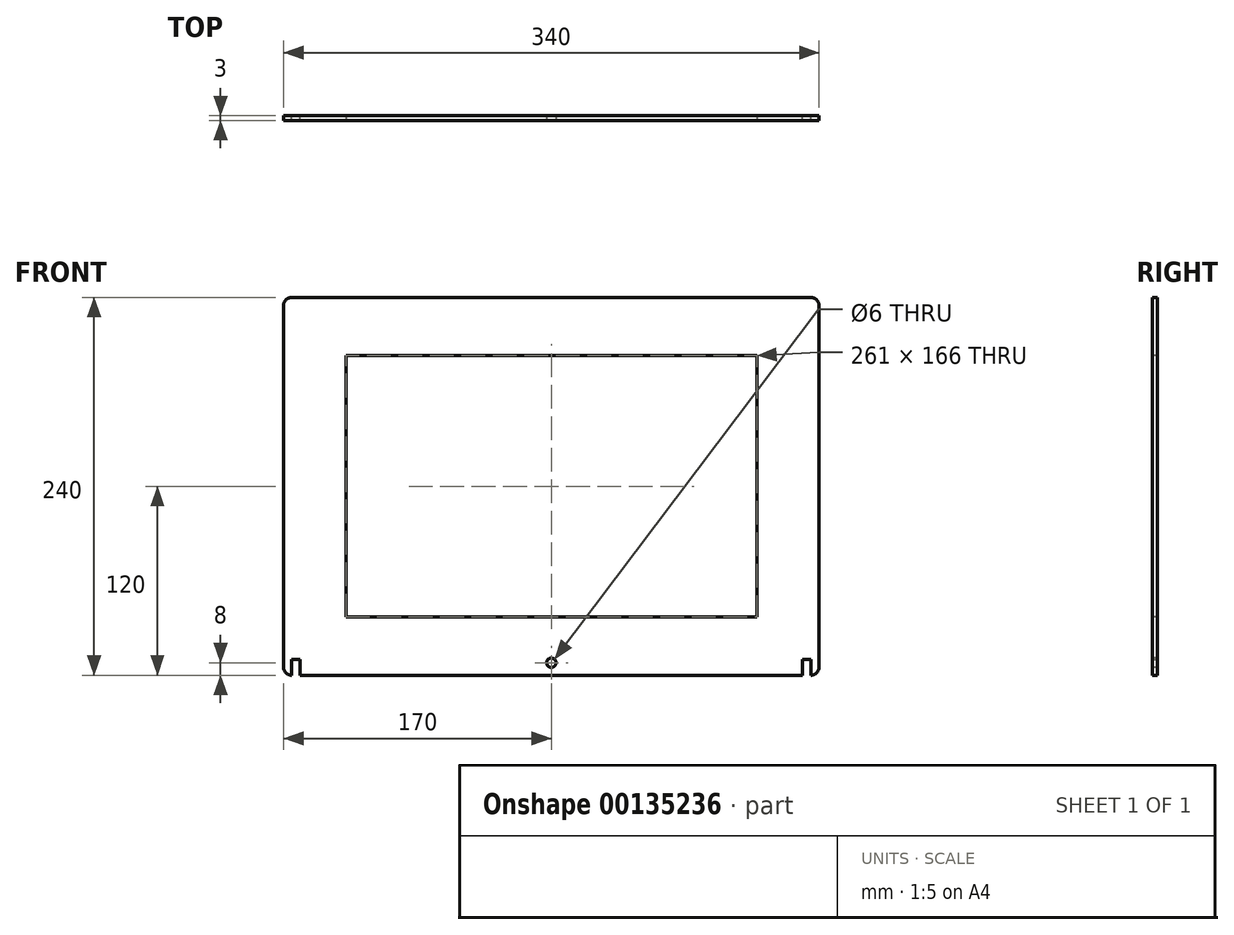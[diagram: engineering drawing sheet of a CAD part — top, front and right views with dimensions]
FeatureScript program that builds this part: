
annotation { "Feature Type Name" : "Feature", "Feature Type Description" : "" }
export const myFeature = defineFeature(function(context is Context, id is Id, definition is map)
    precondition{}
    {
        {
            var Q0;
            Q0=qCreatedBy(makeId("Front.planeOp"),FACE);
            var sketch = newSketch(context, id + "F0", { "sketchPlane" : qUnion([Q0])});
            skLineSegment(sketch, "E0.top", {"start": v(170, 120) * mm, "end": v(-170, 120) * mm});
            skLineSegment(sketch, "E0.left", {"start": v(170, -120) * mm, "end": v(170, 120) * mm});
            skLineSegment(sketch, "E0.right", {"start": v(-170, -120) * mm, "end": v(-170, 120) * mm});
            skPoint(sketch, "E0.middle", {"position": v(0, 0) * mm});
            skLineSegment(sketch, "E1", {"start": v(-165, -120) * mm, "end": v(-165, -110) * mm});
            skLineSegment(sketch, "E2", {"start": v(-165, -110) * mm, "end": v(-159.5, -110) * mm});
            skLineSegment(sketch, "E3", {"start": v(-159.5, -110) * mm, "end": v(-159.5, -120) * mm});
            skLineSegment(sketch, "E4.trimOffspring", {"start": v(-165, -120) * mm, "end": v(-170, -120) * mm});
            skLineSegment(sketch, "E5", {"start": v(165, -120) * mm, "end": v(165, -110) * mm});
            skLineSegment(sketch, "E6", {"start": v(165, -110) * mm, "end": v(159.5, -110) * mm});
            skLineSegment(sketch, "E7", {"start": v(159.5, -110) * mm, "end": v(159.5, -120) * mm});
            skLineSegment(sketch, "E8.trimOffspring", {"start": v(159.5, -120) * mm, "end": v(-159.5, -120) * mm});
            skLineSegment(sketch, "E9", {"start": v(170, -120) * mm, "end": v(165, -120) * mm});
            skSolve(sketch);
        }
        {
            var Q0;
            Q0 = qSketchRegion(id + "F0", true);
            extrude(context, id + "F1", {"entities" : qUnion([Q0]), "depth" : 3 * mm});
        }
        {
            var Q0;
            Q0=makeQuery(id+"F1.opExtrude","CAP_FACE",FACE,{"disambiguationData":[OSD([sQuery(id+"F0.wireOp",EDGE,"E0.bottom"),sQuery(id+"F0.wireOp",EDGE,"E0.top"),sQuery(id+"F0.wireOp",EDGE,"E0.left"),sQuery(id+"F0.wireOp",EDGE,"E0.right"),sQuery(id+"F0.wireOp",EDGE,"E1"),sQuery(id+"F0.wireOp",EDGE,"E2"),sQuery(id+"F0.wireOp",EDGE,"E3"),sQuery(id+"F0.wireOp",EDGE,"E4.trimOffspring"),sQuery(id+"F0.wireOp",EDGE,"E5"),sQuery(id+"F0.wireOp",EDGE,"E6"),sQuery(id+"F0.wireOp",EDGE,"E7"),sQuery(id+"F0.wireOp",EDGE,"E8.trimOffspring")])],"isStart":false});
            var sketch = newSketch(context, id + "F2", { "sketchPlane" : qUnion([Q0])});
            skLineSegment(sketch, "E10.bottom", {"start": v(130.5, -83) * mm, "end": v(-130.5, -83) * mm});
            skLineSegment(sketch, "E10.top", {"start": v(130.5, 83) * mm, "end": v(-130.5, 83) * mm});
            skLineSegment(sketch, "E10.left", {"start": v(130.5, -83) * mm, "end": v(130.5, 83) * mm});
            skLineSegment(sketch, "E10.right", {"start": v(-130.5, -83) * mm, "end": v(-130.5, 83) * mm});
            skPoint(sketch, "E10.middle", {"position": v(0, 0) * mm});
            skCircle(sketch, "E11", {"center": v(0, -112) * mm, "radius": 3 * mm});
            skSolve(sketch);
        }
        {
            var Q0;
            Q0 = qSketchRegion(id + "F2", true);
            extrude(context, id + "F3", {"entities" : qUnion([Q0]), "operationType" : NewBodyOperationType.REMOVE, "endBound" : BoundingType.UP_TO_NEXT, "oppositeDirection" : true, "depth" : 25 * mm});
        }
        {
            var Q0;
            Q0=makeQuery(id+"F1.opExtrude","SWEPT_EDGE",EDGE,{"disambiguationData":[OSD([sQuery(id+"F0.wireOp",EDGE,"E0.top"),sQuery(id+"F0.wireOp",EDGE,"E0.right")])]});
            var Q1;
            Q1=makeQuery(id+"F1.opExtrude","SWEPT_EDGE",EDGE,{"disambiguationData":[OSD([sQuery(id+"F0.wireOp",EDGE,"E0.top"),sQuery(id+"F0.wireOp",EDGE,"E0.left")])]});
            var Q2;
            Q2=makeQuery(id+"F1.opExtrude","SWEPT_EDGE",EDGE,{"disambiguationData":[OSD([sQuery(id+"F0.wireOp",EDGE,"E0.left"),sQuery(id+"F0.wireOp",EDGE,"E9")])]});
            var Q3;
            Q3=makeQuery(id+"F1.opExtrude","SWEPT_EDGE",EDGE,{"disambiguationData":[OSD([sQuery(id+"F0.wireOp",EDGE,"E0.right"),sQuery(id+"F0.wireOp",EDGE,"E4.trimOffspring")])]});
            fillet(context, id + "F4", {"entities" : qUnion([Q0, Q1, Q2, Q3]), "radius" : 5 * mm, "tangentPropagation" : true, "allowEdgeOverflow" : false});
        }
    });
